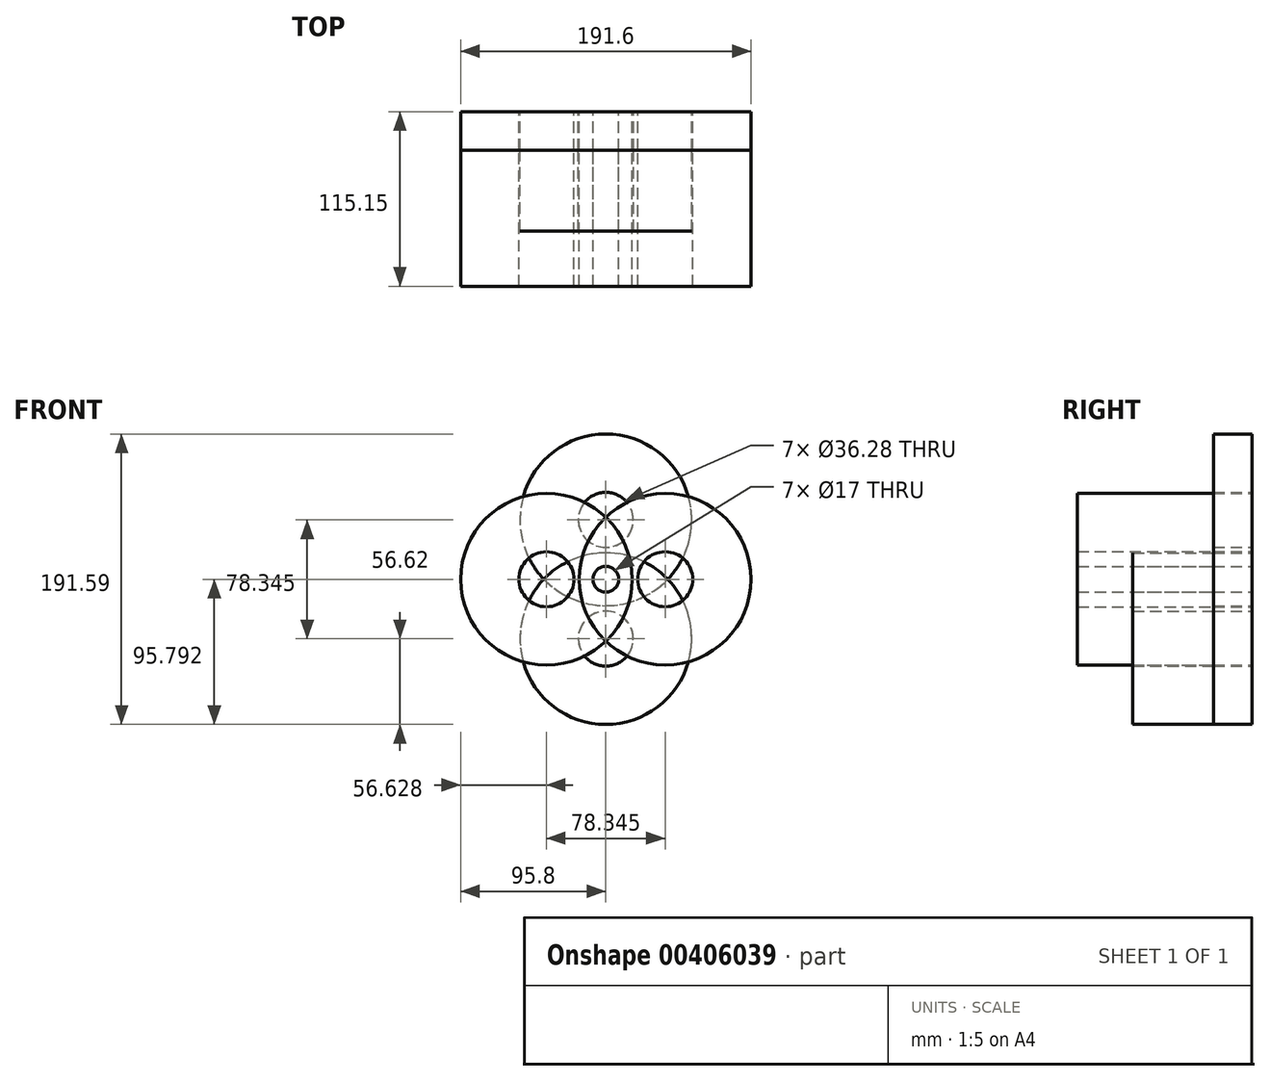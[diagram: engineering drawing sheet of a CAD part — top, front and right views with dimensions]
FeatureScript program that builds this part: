
annotation { "Feature Type Name" : "Feature", "Feature Type Description" : "" }
export const myFeature = defineFeature(function(context is Context, id is Id, definition is map)
    precondition{}
    {
        {
            var Q0;
            Q0=qCreatedBy(makeId("Front.planeOp"),FACE);
            var sketch = newSketch(context, id + "F0", { "sketchPlane" : qUnion([Q0])});
            skCircle(sketch, "E0", {"center": v(0, 0) * mm, "radius": 56.62 * mm});
            skCircle(sketch, "E1", {"center": v(0, 0) * mm, "radius": 18.14 * mm});
            skCircle(sketch, "E2", {"center": v(0, 39.17) * mm, "radius": 8.5 * mm});
            skSolve(sketch);
        }
        {
            var Q0;
            Q0=makeQuery(id+"F0.imprint","IMPRINT",FACE,{"disambiguationData":[TD([[makeQuery(id+"F0.imprint","IMPRINT",EDGE,{"derivedFrom":sQuery(id+"F0.wireOp",EDGE,"E0")}),1.0]])]});
            extrude(context, id + "F1", {"entities" : qUnion([Q0]), "depth" : 25.4 * mm});
        }
        {
            var Q0;
            Q0=makeQuery(id+"F1.opExtrude","SWEPT_BODY",BODY,{"disambiguationData":[OSD([sQuery(id+"F0.wireOp",EDGE,"E0"),sQuery(id+"F0.wireOp",EDGE,"E1"),sQuery(id+"F0.wireOp",EDGE,"E2")])]});
            var Q1;
            Q1=makeQuery(id+"F1.opExtrude","CAP_EDGE",EDGE,{"disambiguationData":[OSD([sQuery(id+"F0.wireOp",EDGE,"E2")])],"isStart":false});
            circularPattern(context, id + "F2", {"entities" : qUnion([Q0]), "axis" : qUnion([Q1]), "angle" : 360 * degree, "instanceCount" : 4, "equalSpace" : true});
        }
        {
            var Q0;
            Q0=makeQuery(id+"F2.opPattern","COPY",FACE,{"derivedFrom":makeQuery(id+"F1.opExtrude","CAP_FACE",FACE,{"disambiguationData":[OSD([sQuery(id+"F0.wireOp",EDGE,"E0"),sQuery(id+"F0.wireOp",EDGE,"E1"),sQuery(id+"F0.wireOp",EDGE,"E2")])],"isStart":false}),"instanceName":"3"});
            var Q1;
            Q1=makeQuery(id+"F2.opPattern","COPY",FACE,{"derivedFrom":makeQuery(id+"F1.opExtrude","CAP_FACE",FACE,{"disambiguationData":[OSD([sQuery(id+"F0.wireOp",EDGE,"E0"),sQuery(id+"F0.wireOp",EDGE,"E1"),sQuery(id+"F0.wireOp",EDGE,"E2")])],"isStart":false}),"instanceName":"1"});
            extrude(context, id + "F3", {"entities" : qUnion([Q0, Q1]), "depth" : 89.75 * mm});
        }
        {
            var Q0;
            Q0=makeQuery(id+"F1.opExtrude","CAP_FACE",FACE,{"disambiguationData":[OSD([sQuery(id+"F0.wireOp",EDGE,"E0"),sQuery(id+"F0.wireOp",EDGE,"E1"),sQuery(id+"F0.wireOp",EDGE,"E2")])],"isStart":false});
            extrude(context, id + "F4", {"entities" : qUnion([Q0]), "depth" : 53.24 * mm});
        }
    });
